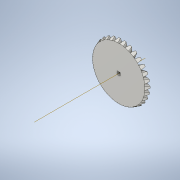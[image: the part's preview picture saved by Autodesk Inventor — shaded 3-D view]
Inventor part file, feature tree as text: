
AUTODESK INVENTOR PART (.ipt)
format: ipt  version: 2022 (Build 260153000, 153)  size: 1,452,032 bytes
history: native  units: in
note: dims shown in document units (in); Inventor stores cm internally (conversion verified against a paired STEP export)
features: other x30, sketch x3, extrude x2, chamfer x1, projected_geometry x1
ambient origin geometry x8: Origin, YZ Plane, XZ Plane, XY Plane, X Axis, Y Axis, Z Axis, Center Point
bodies: Solid1 (feature_tree)
feature tree (37):
  other  "Bevel Gear2"
  extrude  "Extrusion1"  Depth=0.1309in
  extrude  "Extrusion2"  Depth=0.2in
  chamfer  "Chamfer1"  Distance=0.2in
  other  "Solid1::Bevel Gear2"
  other  "TaggingFeature1"
  other  "Teeth Body Sketch"
  other  "Start Sketch"
  other  "End Sketch"
  other  "End Sketch Right"
  other  "End Sketch Left"
  other  "Body Sketch"
  sketch  "Sketch6"  dims[d0=0.3937in]
  other  "3D Sketch Right"
  other  "3D Sketch Left"
  other  "Mesh Plane"
  other  "Top Plane"
  other  "Mesh Plane2"
  other  "Tooth Plane"
  other  "End Plane"
  other  "End Plane Right"
  other  "End Plane Left"
  other  "Z Axis_1"
  other  "Top Point"
  other  "Start Point"
  other  "End Point"
  other  "Srf1"
  sketch  "Sketch8"  dims[d48=0.0in d49=0.0in d50=90.0deg d52=0.0in d53=0.0in d54=0.0in d1=0.1309in]
  sketch  "Sketch9"  dims[d2=0.0in d3=0.0in d4=0.4764in d5=0.2in d6=0.0in d7=0.0472in d8=0.125in d9=45.0deg]
  projected_geometry  "Projected Loop1"
  other  "Srf1::Derived"
  other  "Start plane iMate"
  other  "Mesh iMate2"
  other  "Axis Angle iMate"
  other  "Axis iMate"
  other  "Mesh iMate"
  other  "Intersection iMate"
